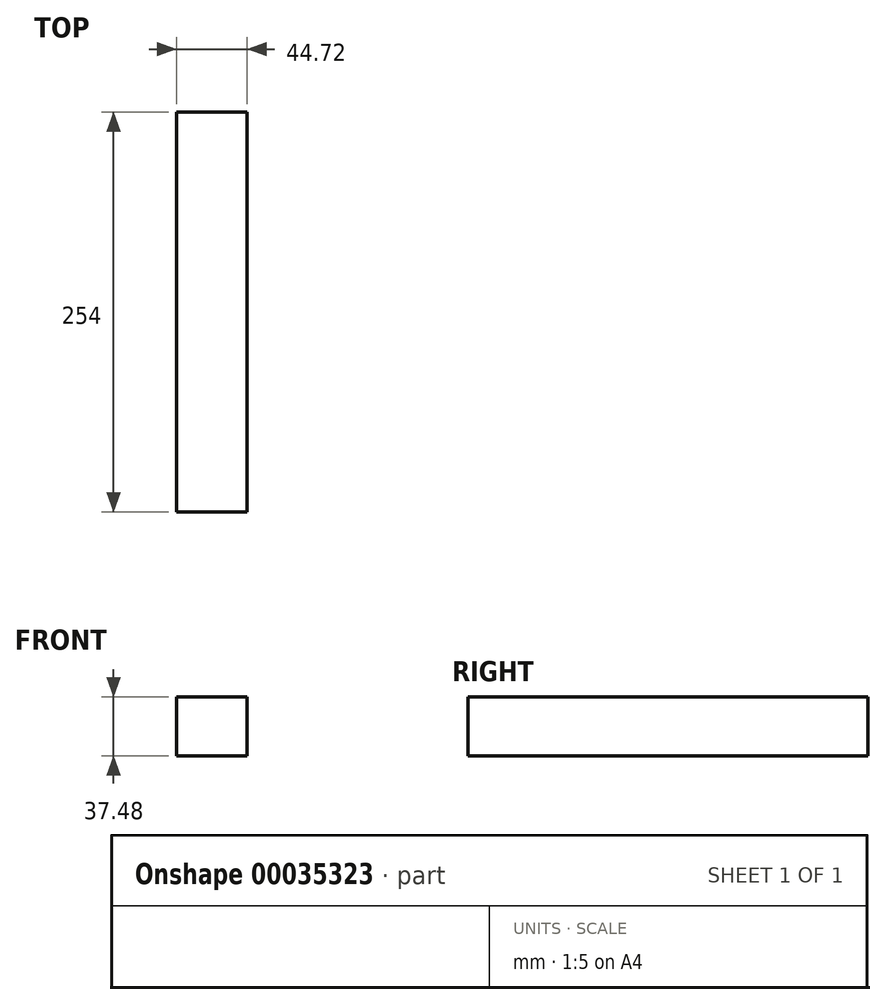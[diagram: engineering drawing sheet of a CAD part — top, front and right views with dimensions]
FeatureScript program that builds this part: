
annotation { "Feature Type Name" : "Feature", "Feature Type Description" : "" }
export const myFeature = defineFeature(function(context is Context, id is Id, definition is map)
    precondition{}
    {
        {
            var Q0;
            Q0=qCreatedBy(makeId("Front.planeOp"),FACE);
            var sketch = newSketch(context, id + "F0", { "sketchPlane" : qUnion([Q0])});
            skLineSegment(sketch, "E0", {"start": v(0, 0) * mm, "end": v(0, 37.48) * mm});
            skLineSegment(sketch, "E1", {"start": v(0, 37.48) * mm, "end": v(44.72, 37.48) * mm});
            skLineSegment(sketch, "E2", {"start": v(44.72, 37.48) * mm, "end": v(44.72, 0) * mm});
            skLineSegment(sketch, "E3", {"start": v(44.72, 0) * mm, "end": v(0, 0) * mm});
            skSolve(sketch);
        }
        {
            var Q0;
            Q0=makeQuery(id+"F0.imprint","IMPRINT",FACE,{"disambiguationData":[TD([[makeQuery(id+"F0.imprint","IMPRINT",EDGE,{"derivedFrom":sQuery(id+"F0.wireOp",EDGE,"E0")}),-1.0]])]});
            extrude(context, id + "F1", {"entities" : qUnion([Q0]), "depth" : 254 * mm});
        }
    });
